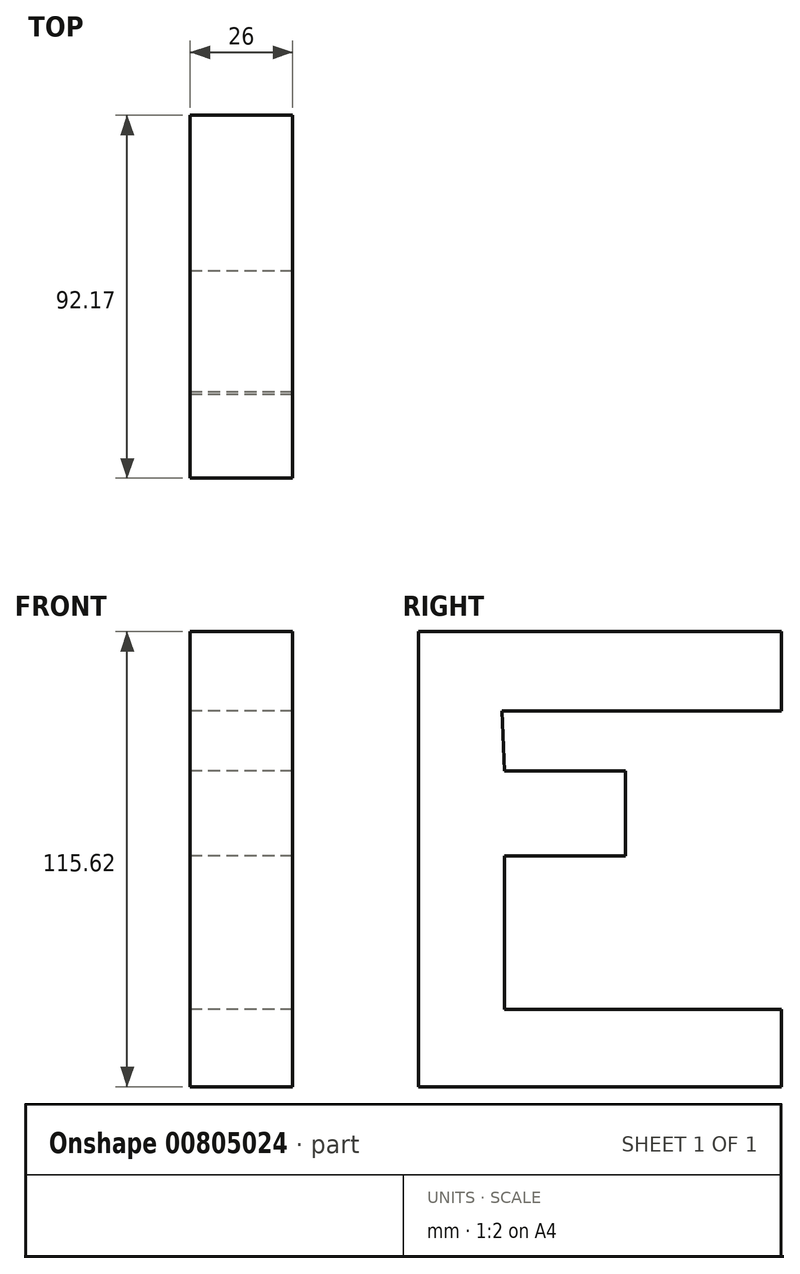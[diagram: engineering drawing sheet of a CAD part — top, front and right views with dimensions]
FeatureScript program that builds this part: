
annotation { "Feature Type Name" : "Feature", "Feature Type Description" : "" }
export const myFeature = defineFeature(function(context is Context, id is Id, definition is map)
    precondition{}
    {
        {
            var Q0;
            Q0=qCreatedBy(makeId("Right.planeOp"),FACE);
            var sketch = newSketch(context, id + "F0", { "sketchPlane" : qUnion([Q0])});
            skLineSegment(sketch, "E0", {"start": v(-52.63, 57) * mm, "end": v(-52.63, -58.63) * mm});
            skLineSegment(sketch, "E1", {"start": v(-52.63, 57) * mm, "end": v(39.54, 57) * mm});
            skLineSegment(sketch, "E2", {"start": v(-52.63, -58.63) * mm, "end": v(39.54, -58.63) * mm});
            skLineSegment(sketch, "E3", {"start": v(39.54, 57) * mm, "end": v(39.54, 36.81) * mm});
            skLineSegment(sketch, "E4", {"start": v(39.54, -58.63) * mm, "end": v(39.54, -39) * mm});
            skLineSegment(sketch, "E5", {"start": v(39.54, -39) * mm, "end": v(-30.81, -39) * mm});
            skLineSegment(sketch, "E6", {"start": v(39.54, 36.81) * mm, "end": v(-31.36, 36.81) * mm});
            skLineSegment(sketch, "E7", {"start": v(-30.81, -39) * mm, "end": v(-30.81, 0) * mm});
            skLineSegment(sketch, "E8", {"start": v(-30.81, 0) * mm, "end": v(0, 0) * mm});
            skLineSegment(sketch, "E9", {"start": v(0, 0) * mm, "end": v(0, 21.54) * mm});
            skLineSegment(sketch, "E10", {"start": v(0, 21.54) * mm, "end": v(-30.81, 21.54) * mm});
            skLineSegment(sketch, "E11", {"start": v(-31.36, 36.81) * mm, "end": v(-30.81, 21.54) * mm});
            skSolve(sketch);
        }
        {
            var Q0;
            Q0 = qSketchRegion(id + "F0", true);
            extrude(context, id + "F1", {"entities" : qUnion([Q0]), "depth" : 26 * mm, "offsetDistance" : 25 * mm});
        }
    });
